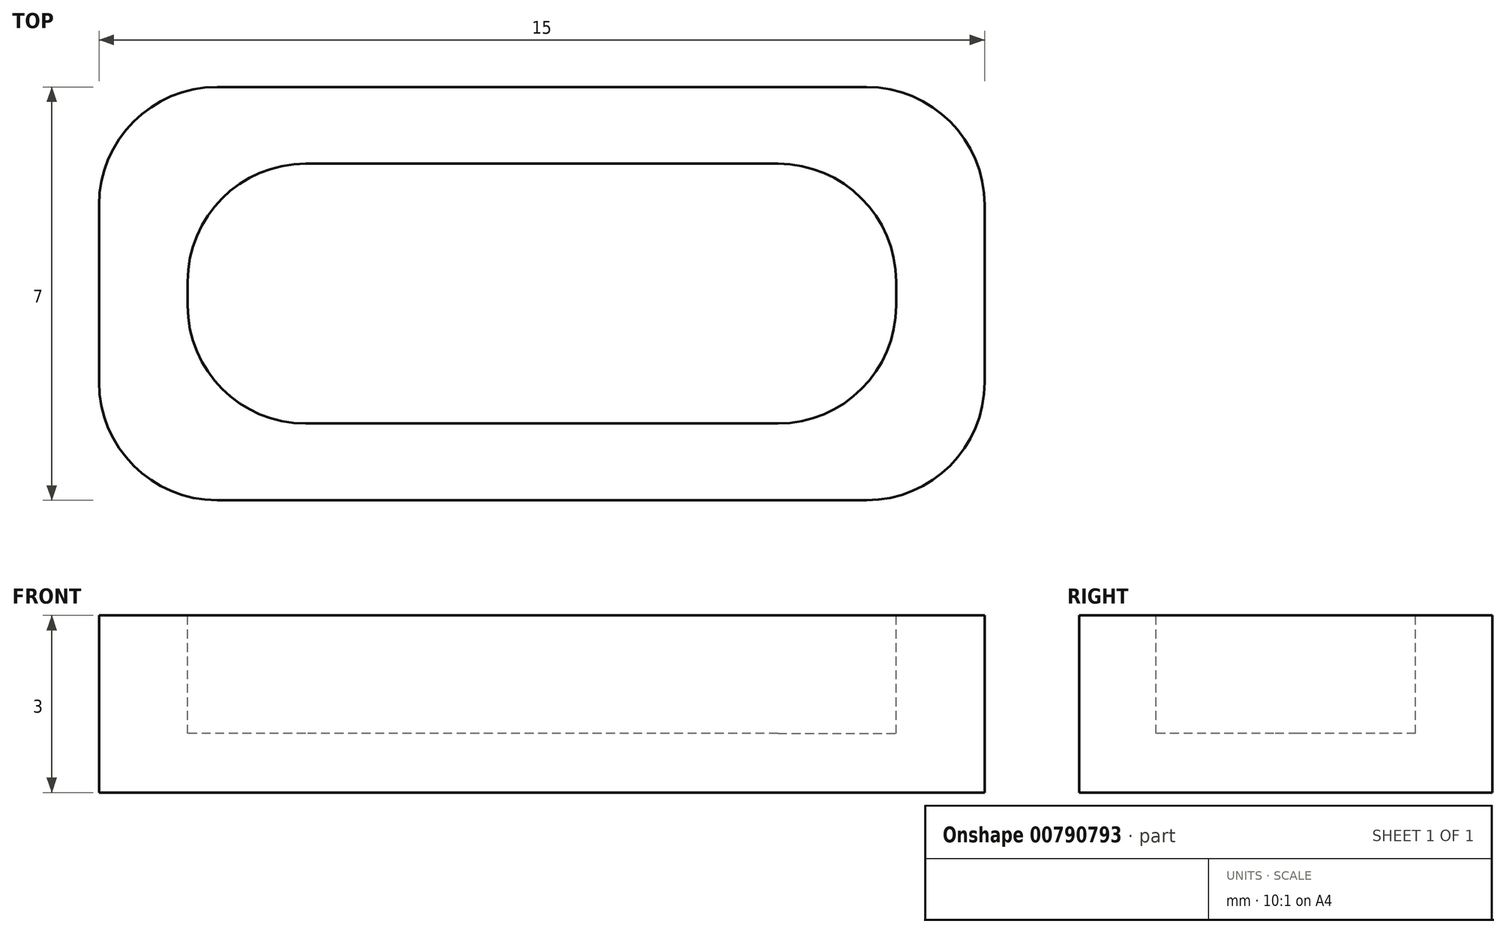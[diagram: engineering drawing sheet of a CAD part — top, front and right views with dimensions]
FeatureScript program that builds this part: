
annotation { "Feature Type Name" : "Feature", "Feature Type Description" : "" }
export const myFeature = defineFeature(function(context is Context, id is Id, definition is map)
    precondition{}
    {
        {
            var Q0;
            Q0=qCreatedBy(makeId("Top.planeOp"),FACE);
            var sketch = newSketch(context, id + "F0", { "sketchPlane" : qUnion([Q0])});
            skLineSegment(sketch, "E0.bottom", {"start": v(5.5, 3.5) * mm, "end": v(-5.5, 3.5) * mm});
            skLineSegment(sketch, "E0.top", {"start": v(5.5, -3.5) * mm, "end": v(-5.5, -3.5) * mm});
            skLineSegment(sketch, "E0.left", {"start": v(7.5, 1.5) * mm, "end": v(7.5, -1.5) * mm});
            skLineSegment(sketch, "E0.right", {"start": v(-7.5, 1.5) * mm, "end": v(-7.5, -1.5) * mm});
            skPoint(sketch, "E0.middle", {"position": v(0, 0) * mm});
            skPoint(sketch, "E1.visualSharp", {"position": v(-7.5, 3.5) * mm});
            skArc(sketch, "E1.filletArc", {"start": v(-5.5, 3.5) * mm, "mid": v(-6.91, 2.91) * mm, "end": v(-7.5, 1.5) * mm});
            skPoint(sketch, "E2.visualSharp", {"position": v(-7.5, -3.5) * mm});
            skArc(sketch, "E2.filletArc", {"start": v(-7.5, -1.5) * mm, "mid": v(-6.91, -2.91) * mm, "end": v(-5.5, -3.5) * mm});
            skPoint(sketch, "E3.visualSharp", {"position": v(7.5, 3.5) * mm});
            skArc(sketch, "E3.filletArc", {"start": v(7.5, 1.5) * mm, "mid": v(6.91, 2.91) * mm, "end": v(5.5, 3.5) * mm});
            skPoint(sketch, "E4.visualSharp", {"position": v(7.5, -3.5) * mm});
            skArc(sketch, "E4.filletArc", {"start": v(5.5, -3.5) * mm, "mid": v(6.91, -2.91) * mm, "end": v(7.5, -1.5) * mm});
            skSolve(sketch);
        }
        {
            var Q0;
            Q0=makeQuery(id+"F0.imprint","IMPRINT",FACE,{"disambiguationData":[TD([[makeQuery(id+"F0.imprint","IMPRINT",EDGE,{"derivedFrom":sQuery(id+"F0.wireOp",EDGE,"E0.bottom")}),1.0]])]});
            extrude(context, id + "F1", {"entities" : qUnion([Q0]), "depth" : 3 * mm, "offsetDistance" : 25 * mm});
        }
        {
            var Q0;
            Q0=makeQuery(id+"F1.opExtrude","CAP_FACE",FACE,{"disambiguationData":[OSD([sQuery(id+"F0.wireOp",EDGE,"E0.bottom"),sQuery(id+"F0.wireOp",EDGE,"E0.top"),sQuery(id+"F0.wireOp",EDGE,"E0.left"),sQuery(id+"F0.wireOp",EDGE,"E0.right")])],"isStart":false});
            var sketch = newSketch(context, id + "F2", { "sketchPlane" : qUnion([Q0])});
            skLineSegment(sketch, "E5.bottom", {"start": v(4, 2.2) * mm, "end": v(-4, 2.2) * mm});
            skLineSegment(sketch, "E5.top", {"start": v(4, -2.2) * mm, "end": v(-4, -2.2) * mm});
            skLineSegment(sketch, "E5.left", {"start": v(6, 0.2) * mm, "end": v(6, -0.2) * mm});
            skLineSegment(sketch, "E5.right", {"start": v(-6, 0.2) * mm, "end": v(-6, -0.2) * mm});
            skPoint(sketch, "E5.middle", {"position": v(0, 0) * mm});
            skPoint(sketch, "E6.visualSharp", {"position": v(-6, 2.2) * mm});
            skArc(sketch, "E6.filletArc", {"start": v(-4, 2.2) * mm, "mid": v(-5.41, 1.61) * mm, "end": v(-6, 0.2) * mm});
            skPoint(sketch, "E7.visualSharp", {"position": v(-6, -2.2) * mm});
            skArc(sketch, "E7.filletArc", {"start": v(-6, -0.2) * mm, "mid": v(-5.41, -1.61) * mm, "end": v(-4, -2.2) * mm});
            skPoint(sketch, "E8.visualSharp", {"position": v(6, 2.2) * mm});
            skArc(sketch, "E8.filletArc", {"start": v(6, 0.2) * mm, "mid": v(5.41, 1.61) * mm, "end": v(4, 2.2) * mm});
            skPoint(sketch, "E9.visualSharp", {"position": v(6, -2.2) * mm});
            skArc(sketch, "E9.filletArc", {"start": v(4, -2.2) * mm, "mid": v(5.41, -1.61) * mm, "end": v(6, -0.2) * mm});
            skSolve(sketch);
        }
        {
            var Q0;
            Q0=makeQuery(id+"F2.imprint","IMPRINT",FACE,{"disambiguationData":[TD([[makeQuery(id+"F2.imprint","IMPRINT",EDGE,{"derivedFrom":sQuery(id+"F2.wireOp",EDGE,"E5.bottom")}),1.0]])]});
            extrude(context, id + "F3", {"entities" : qUnion([Q0]), "operationType" : NewBodyOperationType.ADD, "oppositeDirection" : true, "depth" : 2 * mm, "offsetDistance" : 25 * mm});
        }
        {
            var Q0;
            Q0 = qSketchRegion(id + "F2", true);
            extrude(context, id + "F4", {"entities" : qUnion([Q0]), "operationType" : NewBodyOperationType.REMOVE, "oppositeDirection" : true, "depth" : 2 * mm, "offsetDistance" : 25 * mm});
        }
    });
